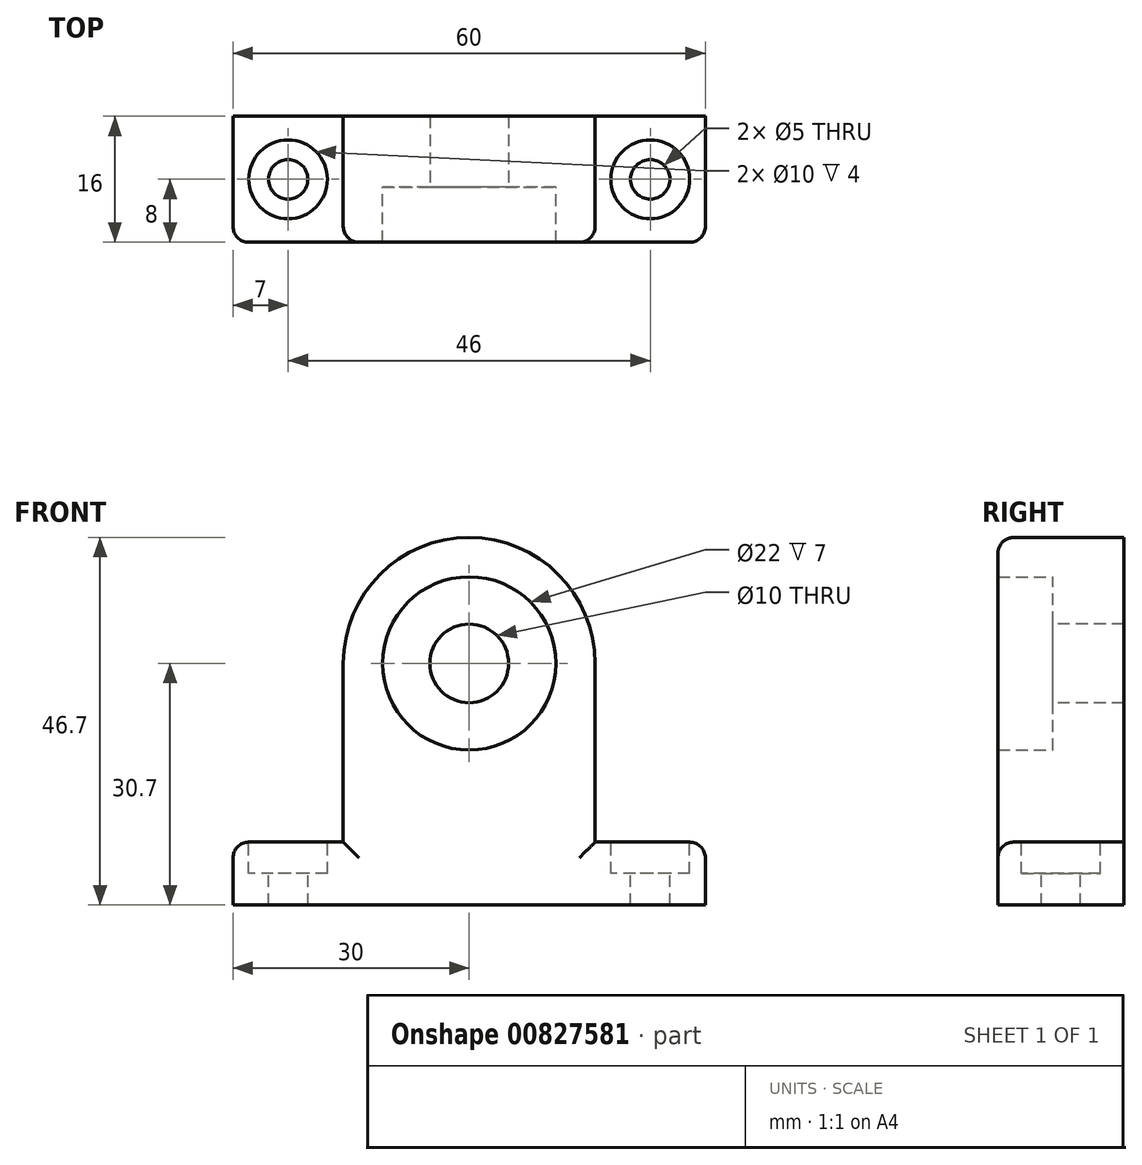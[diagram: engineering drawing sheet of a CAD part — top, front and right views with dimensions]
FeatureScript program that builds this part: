
annotation { "Feature Type Name" : "Feature", "Feature Type Description" : "" }
export const myFeature = defineFeature(function(context is Context, id is Id, definition is map)
    precondition{}
    {
        {
            var Q0;
            Q0=qCreatedBy(makeId("Front.planeOp"),FACE);
            var sketch = newSketch(context, id + "F0", { "sketchPlane" : qUnion([Q0])});
            skCircle(sketch, "E0", {"center": v(0, 30.7) * mm, "radius": 11 * mm});
            skArc(sketch, "E1", {"start": v(16, 30.7) * mm, "mid": v(0, 46.7) * mm, "end": v(-16, 30.7) * mm});
            skLineSegment(sketch, "E2.bottom", {"start": v(-30, 8) * mm, "end": v(-16, 8) * mm});
            skLineSegment(sketch, "E2.left", {"start": v(-30, 8) * mm, "end": v(-30, 0) * mm});
            skLineSegment(sketch, "E2.right", {"start": v(30, 8) * mm, "end": v(30, 0) * mm});
            skPoint(sketch, "E2.middle", {"position": v(0, 0) * mm});
            skLineSegment(sketch, "E3.0", {"start": v(-30, 0) * mm, "end": v(30, 0) * mm});
            skLineSegment(sketch, "E4.0", {"start": v(16, 8) * mm, "end": v(16, 30.7) * mm});
            skLineSegment(sketch, "E5.0", {"start": v(-16, 8) * mm, "end": v(-16, 30.7) * mm});
            skLineSegment(sketch, "E6.trimOffspring", {"start": v(16, 8) * mm, "end": v(30, 8) * mm});
            skSolve(sketch);
        }
        {
            var Q0;
            Q0=makeQuery(id+"F0.imprint","IMPRINT",FACE,{"disambiguationData":[TD([[makeQuery(id+"F0.imprint","IMPRINT",EDGE,{"derivedFrom":sQuery(id+"F0.wireOp",EDGE,"E0")}),-1.0]])]});
            extrude(context, id + "F1", {"entities" : qUnion([Q0]), "endBound" : BoundingType.SYMMETRIC, "depth" : 16 * mm, "offsetDistance" : 25 * mm});
        }
        {
            var Q0;
            Q0=makeQuery(id+"F1.opExtrude","CAP_FACE",FACE,{"disambiguationData":[OSD([sQuery(id+"F0.wireOp",EDGE,"E0"),sQuery(id+"F0.wireOp",EDGE,"E1"),sQuery(id+"F0.wireOp",EDGE,"E2.bottom"),sQuery(id+"F0.wireOp",EDGE,"E2.left"),sQuery(id+"F0.wireOp",EDGE,"E2.right"),sQuery(id+"F0.wireOp",EDGE,"E3.0"),sQuery(id+"F0.wireOp",EDGE,"E4.0"),sQuery(id+"F0.wireOp",EDGE,"E5.0"),sQuery(id+"F0.wireOp",EDGE,"E6.trimOffspring")])],"isStart":false});
            cPlane(context, id + "F2", {"entities" : qUnion([Q0]), "cplaneType" : CPlaneType.OFFSET, "offset" : 7 * mm, "oppositeDirection" : true, "width" : 150 * mm, "height" : 150 * mm});
        }
        {
            var Q0;
            Q0=qCreatedBy(id+"F2.planeOp",FACE);
            var sketch = newSketch(context, id + "F3", { "sketchPlane" : qUnion([Q0])});
            skCircle(sketch, "E7", {"center": v(0, 30.7) * mm, "radius": 5 * mm});
            skCircle(sketch, "E8", {"center": v(0, 30.7) * mm, "radius": 11.46 * mm});
            skSolve(sketch);
        }
        {
            var Q0;
            Q0=qSketchRegion(id+"F3",true);
            extrude(context, id + "F4", {"entities" : qUnion([Q0]), "operationType" : NewBodyOperationType.ADD, "oppositeDirection" : true, "depth" : 9 * mm, "offsetDistance" : 25 * mm});
        }
        {
            var Q0;
            Q0=makeQuery(id+"F1.opExtrude","SWEPT_FACE",FACE,{"disambiguationData":[OSD([sQuery(id+"F0.wireOp",EDGE,"E6.trimOffspring")])]});
            var sketch = newSketch(context, id + "F5", { "sketchPlane" : qUnion([Q0])});
            skCircle(sketch, "E9", {"center": v(0, 0) * mm, "radius": 23 * mm, "construction": true});
            skLineSegment(sketch, "E10", {"start": v(-38.64, 0) * mm, "end": v(38.82, 0) * mm, "construction": true});
            skPoint(sketch, "E11", {"position": v(-23, 0) * mm});
            skPoint(sketch, "E12", {"position": v(23, 0) * mm});
            skSolve(sketch);
        }
        {
            var Q0;
            Q0=sQuery(id+"F5.wireOp",VERTEX,"E11");
            var Q1;
            Q1=sQuery(id+"F5.wireOp",VERTEX,"E12");
            var Q2;
            Q2=makeQuery(id+"F1.opExtrude","SWEPT_BODY",BODY,{"disambiguationData":[OSD([sQuery(id+"F0.wireOp",EDGE,"E0"),sQuery(id+"F0.wireOp",EDGE,"E1"),sQuery(id+"F0.wireOp",EDGE,"E2.bottom"),sQuery(id+"F0.wireOp",EDGE,"E2.left"),sQuery(id+"F0.wireOp",EDGE,"E2.right"),sQuery(id+"F0.wireOp",EDGE,"E3.0"),sQuery(id+"F0.wireOp",EDGE,"E4.0"),sQuery(id+"F0.wireOp",EDGE,"E5.0"),sQuery(id+"F0.wireOp",EDGE,"E6.trimOffspring")])]});
            hole(context, id + "F6", {"style" : HoleStyle.C_BORE, "endStyle" : HoleEndStyle.THROUGH, "holeDiameter" : 5 * mm, "cBoreDiameter" : 10 * mm, "cBoreDepth" : 4 * mm, "majorDiameter" : 5 * mm, "isTappedThrough" : true, "tappedDepth" : 8 * mm, "tapClearance" : 3, "locations" : qUnion([Q0, Q1]), "scope" : qUnion([Q2])});
        }
        {
            var Q0;
            Q0=makeQuery(id+"F1.opExtrude","CAP_EDGE",EDGE,{"disambiguationData":[OSD([sQuery(id+"F0.wireOp",EDGE,"E2.left")])],"isStart":false});
            var Q1;
            Q1=makeQuery(id+"F1.opExtrude","CAP_EDGE",EDGE,{"disambiguationData":[OSD([sQuery(id+"F0.wireOp",EDGE,"E2.bottom")])],"isStart":false});
            var Q2;
            Q2=makeQuery(id+"F1.opExtrude","CAP_EDGE",EDGE,{"disambiguationData":[OSD([sQuery(id+"F0.wireOp",EDGE,"E5.0")])],"isStart":false});
            var Q3;
            Q3=makeQuery(id+"F1.opExtrude","CAP_EDGE",EDGE,{"disambiguationData":[OSD([sQuery(id+"F0.wireOp",EDGE,"E6.trimOffspring")])],"isStart":false});
            var Q4;
            Q4=makeQuery(id+"F1.opExtrude","CAP_EDGE",EDGE,{"disambiguationData":[OSD([sQuery(id+"F0.wireOp",EDGE,"E2.right")])],"isStart":false});
            var Q5;
            Q5=makeQuery(id+"F1.opExtrude","SWEPT_EDGE",EDGE,{"disambiguationData":[OSD([sQuery(id+"F0.wireOp",EDGE,"E2.bottom"),sQuery(id+"F0.wireOp",EDGE,"E2.left")])]});
            var Q6;
            Q6=makeQuery(id+"F1.opExtrude","SWEPT_EDGE",EDGE,{"disambiguationData":[OSD([sQuery(id+"F0.wireOp",EDGE,"E2.right"),sQuery(id+"F0.wireOp",EDGE,"E6.trimOffspring")])]});
            fillet(context, id + "F7", {"entities" : qUnion([Q0, Q1, Q2, Q3, Q4, Q5, Q6]), "radius" : 2 * mm, "tangentPropagation" : true, "allowEdgeOverflow" : false});
        }
    });
